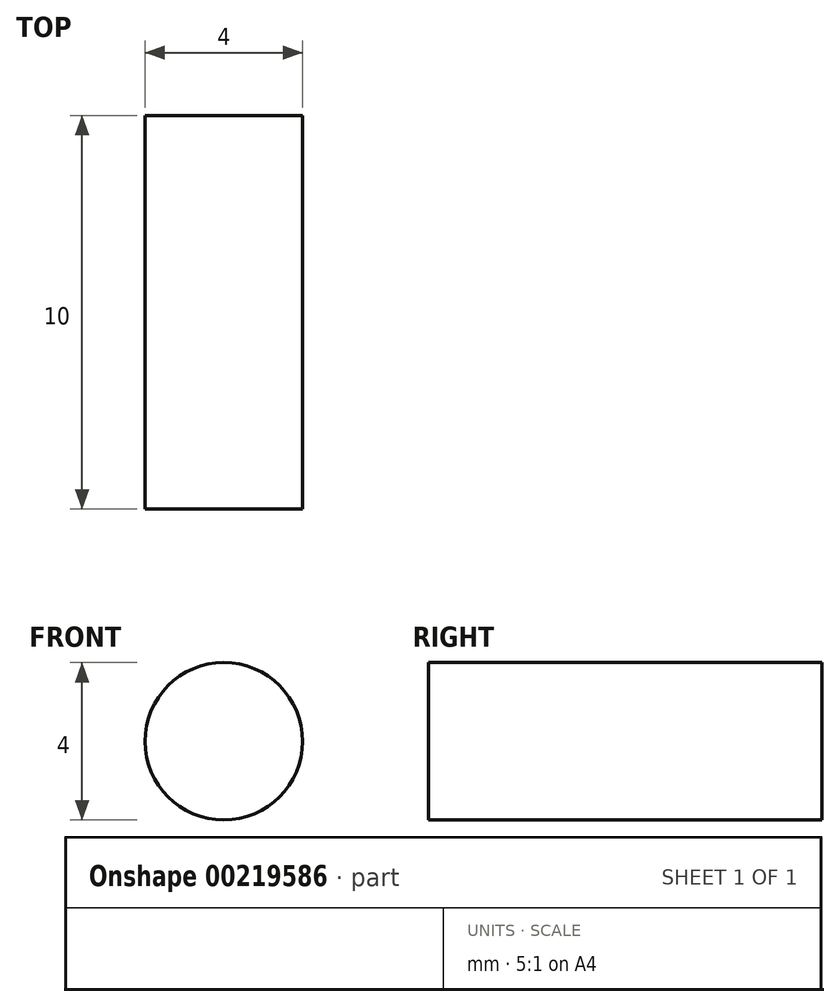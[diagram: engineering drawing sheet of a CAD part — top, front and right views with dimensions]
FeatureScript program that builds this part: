
annotation { "Feature Type Name" : "Feature", "Feature Type Description" : "" }
export const myFeature = defineFeature(function(context is Context, id is Id, definition is map)
    precondition{}
    {
        {
            var Q0;
            Q0=qCreatedBy(makeId("Front.planeOp"),FACE);
            var sketch = newSketch(context, id + "F0", { "sketchPlane" : qUnion([Q0])});
            skCircle(sketch, "E0", {"center": v(0, 0) * mm, "radius": 2 * mm});
            skSolve(sketch);
        }
        {
            var Q0;
            Q0=makeQuery(id+"F0.imprint","IMPRINT",FACE,{"disambiguationData":[TD([[makeQuery(id+"F0.imprint","IMPRINT",EDGE,{"derivedFrom":sQuery(id+"F0.wireOp",EDGE,"E0")}),1.0]])]});
            var Q1;
            Q1=sQuery(id+"F0.wireOp",EDGE,"E0");
            extrude(context, id + "F1", {"entities" : qUnion([Q0]), "surfaceEntities" : qUnion([Q1]), "depth" : 10 * mm});
        }
    });
